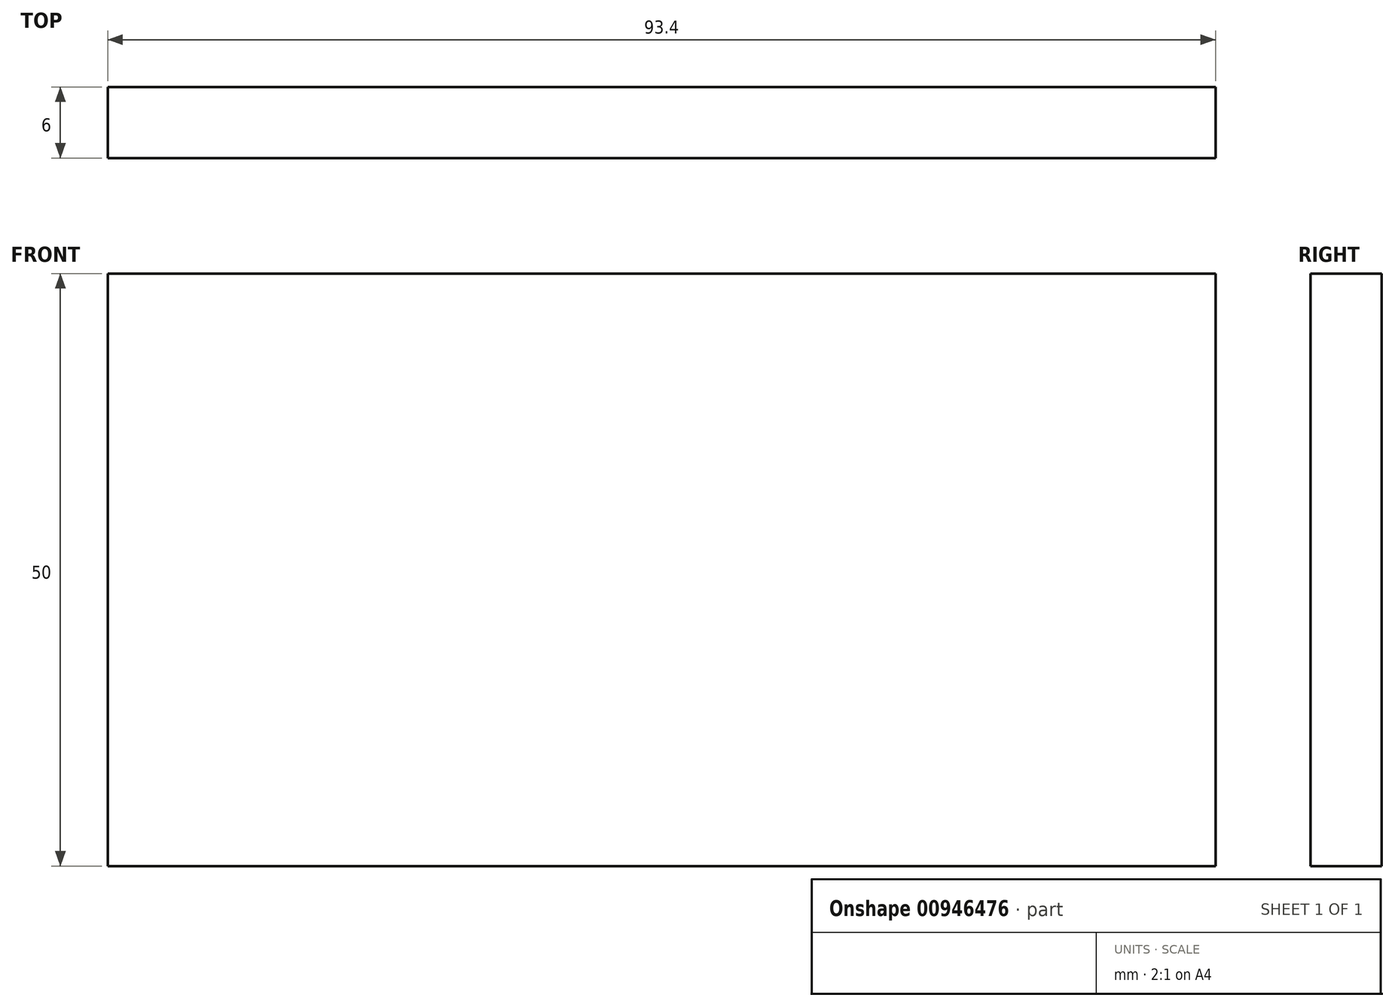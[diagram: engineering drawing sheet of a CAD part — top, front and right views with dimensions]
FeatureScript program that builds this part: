
annotation { "Feature Type Name" : "Feature", "Feature Type Description" : "" }
export const myFeature = defineFeature(function(context is Context, id is Id, definition is map)
    precondition{}
    {
        {
            var Q0;
            Q0=qCreatedBy(makeId("Front.planeOp"),FACE);
            var sketch = newSketch(context, id + "F0", { "sketchPlane" : qUnion([Q0])});
            skLineSegment(sketch, "E0.bottom", {"start": v(46.7, 25) * mm, "end": v(-46.7, 25) * mm});
            skLineSegment(sketch, "E0.top", {"start": v(46.7, -25) * mm, "end": v(-46.7, -25) * mm});
            skLineSegment(sketch, "E0.left", {"start": v(46.7, 25) * mm, "end": v(46.7, -25) * mm});
            skLineSegment(sketch, "E0.right", {"start": v(-46.7, 25) * mm, "end": v(-46.7, -25) * mm});
            skPoint(sketch, "E0.middle", {"position": v(0, 0) * mm});
            skSolve(sketch);
        }
        {
            var Q0;
            Q0=makeQuery(id+"F0.imprint","IMPRINT",FACE,{"disambiguationData":[TD([[makeQuery(id+"F0.imprint","IMPRINT",EDGE,{"derivedFrom":sQuery(id+"F0.wireOp",EDGE,"E0.bottom")}),1.0]])]});
            extrude(context, id + "F1", {"entities" : qUnion([Q0]), "depth" : 6 * mm, "offsetDistance" : 25 * mm});
        }
    });
